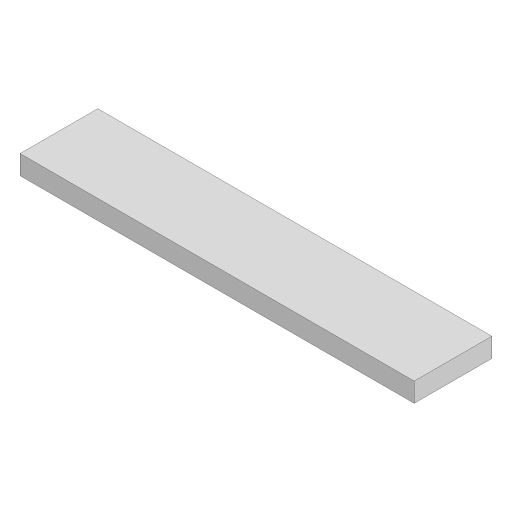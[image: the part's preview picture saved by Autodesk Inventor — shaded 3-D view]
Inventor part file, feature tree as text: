
AUTODESK INVENTOR PART (.ipt)
format: ipt  version: 2024 (Build 280153000, 153)  size: 81,920 bytes
history: native  units: in
note: dims shown in document units (in); Inventor stores cm internally (conversion verified against a paired STEP export)
features: extrude x1, sketch x1
ambient origin geometry x8: Origin, YZ Plane, XZ Plane, XY Plane, X Axis, Y Axis, Z Axis, Center Point
bodies: Solid1 (feature_tree)
feature tree (2):
  extrude  "Extrusion1"  Depth=10.315in
  sketch  "Sketch1"  dims[d0=2.5591in d1=10.315in d2=52.3425in d3=0.0in]
